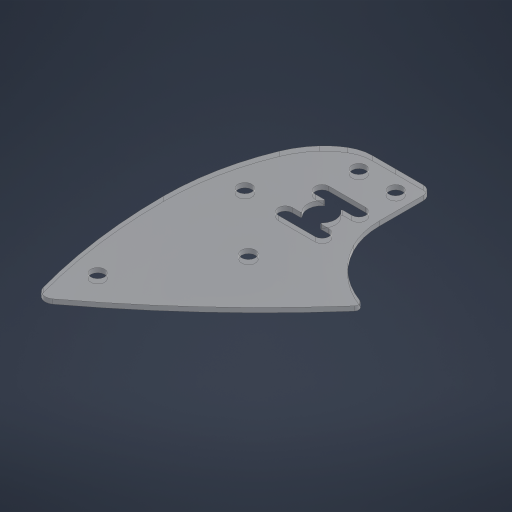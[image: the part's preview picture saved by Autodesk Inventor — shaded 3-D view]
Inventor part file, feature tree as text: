
AUTODESK INVENTOR PART (.ipt)
format: ipt  version: 2024 (Build 280153000, 153)  size: 275,968 bytes
history: native  units: in
note: dims shown in document units (in); Inventor stores cm internally (conversion verified against a paired STEP export)
features: other x3, sketch x1
ambient origin geometry x8: Origin, YZ Plane, XZ Plane, XY Plane, X Axis, Y Axis, Z Axis, Center Point
bodies: Solid1 (feature_tree)
feature tree (4):
  other  "sled2.ipt"
  other  "Solid1::sled2.ipt"
  other  "TaggingFeature1"
  sketch  "Sketch3"  dims[d0=0.3937in]
